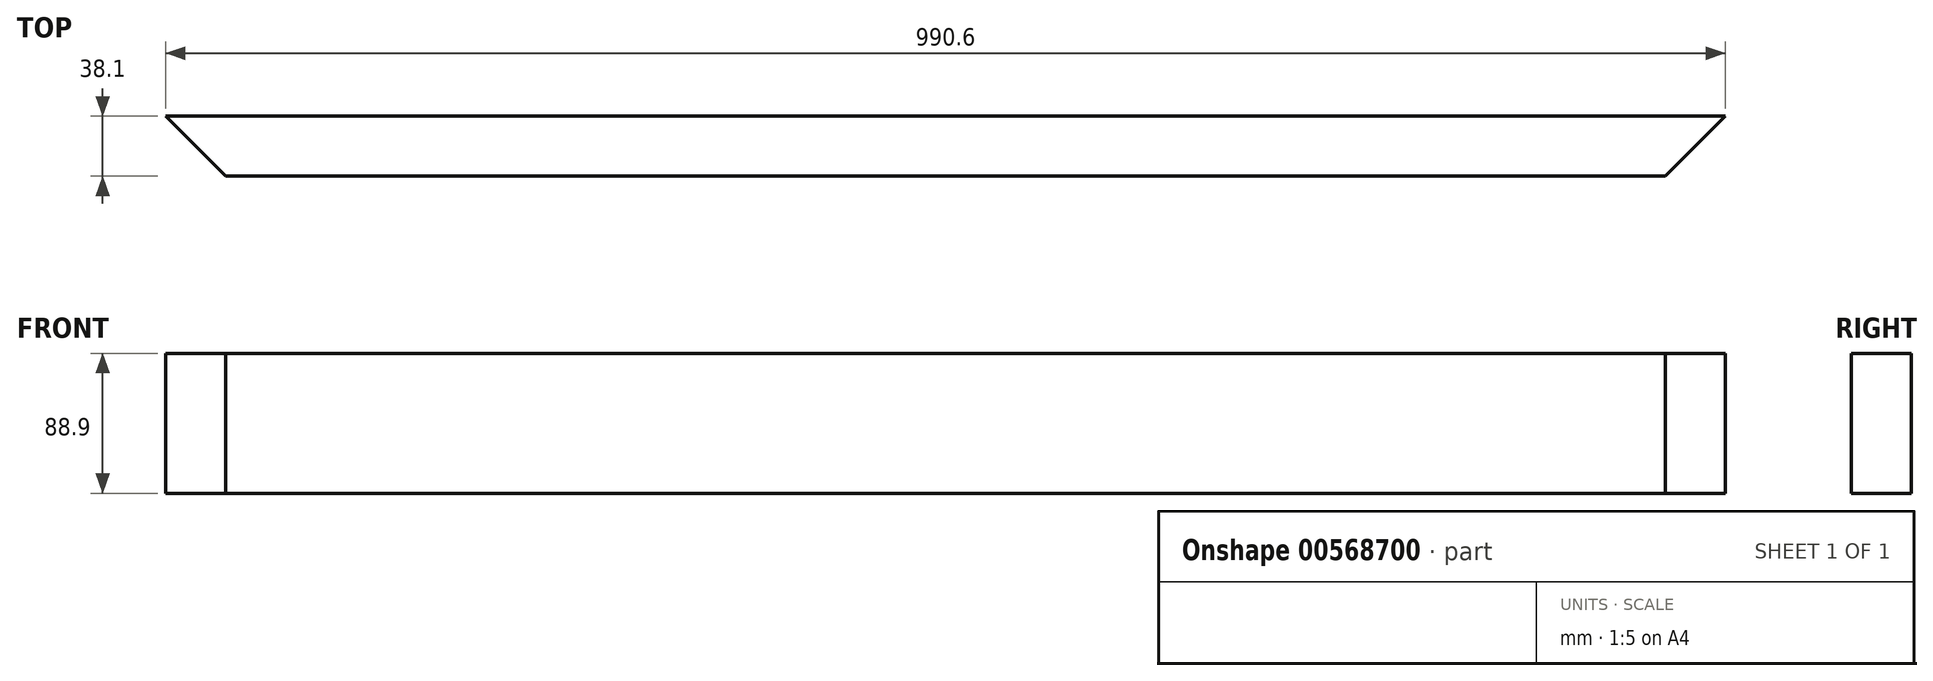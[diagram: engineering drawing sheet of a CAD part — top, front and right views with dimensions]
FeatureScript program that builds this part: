
annotation { "Feature Type Name" : "Feature", "Feature Type Description" : "" }
export const myFeature = defineFeature(function(context is Context, id is Id, definition is map)
    precondition{}
    {
        {
            var Q0;
            Q0=qCreatedBy(makeId("Front.planeOp"),FACE);
            var sketch = newSketch(context, id + "F0", { "sketchPlane" : qUnion([Q0])});
            skLineSegment(sketch, "E0.bottom", {"start": v(-495.3, -44.45) * mm, "end": v(495.3, -44.45) * mm});
            skLineSegment(sketch, "E0.top", {"start": v(-495.3, 44.45) * mm, "end": v(495.3, 44.45) * mm});
            skLineSegment(sketch, "E0.left", {"start": v(-495.3, -44.45) * mm, "end": v(-495.3, 44.45) * mm});
            skLineSegment(sketch, "E0.right", {"start": v(495.3, -44.45) * mm, "end": v(495.3, 44.45) * mm});
            skPoint(sketch, "E0.middle", {"position": v(0, 0) * mm});
            skSolve(sketch);
        }
        {
            var Q0;
            Q0 = qSketchRegion(id + "F0", true);
            extrude(context, id + "F1", {"entities" : qUnion([Q0]), "depth" : 38.1 * mm, "offsetDistance" : 25.4 * mm});
        }
        {
            var Q0;
            Q0=makeQuery(id+"F1.opExtrude","SWEPT_FACE",FACE,{"disambiguationData":[OSD([sQuery(id+"F0.wireOp",EDGE,"E0.top")])]});
            var sketch = newSketch(context, id + "F2", { "sketchPlane" : qUnion([Q0])});
            skLineSegment(sketch, "E1", {"start": v(-495.3, 0) * mm, "end": v(-457.2, -38.1) * mm});
            skLineSegment(sketch, "E2", {"start": v(-457.2, -38.1) * mm, "end": v(-495.3, -38.1) * mm});
            skLineSegment(sketch, "E3", {"start": v(-495.3, -38.1) * mm, "end": v(-495.3, 0) * mm});
            skLineSegment(sketch, "E4", {"start": v(495.3, 0) * mm, "end": v(457.2, -38.1) * mm});
            skLineSegment(sketch, "E5", {"start": v(457.2, -38.1) * mm, "end": v(495.3, -38.1) * mm});
            skLineSegment(sketch, "E6", {"start": v(495.3, -38.1) * mm, "end": v(495.3, 0) * mm});
            skSolve(sketch);
        }
        {
            var Q0;
            Q0 = qSketchRegion(id + "F2", true);
            extrude(context, id + "F3", {"entities" : qUnion([Q0]), "operationType" : NewBodyOperationType.REMOVE, "endBound" : BoundingType.THROUGH_ALL, "oppositeDirection" : true, "depth" : 25.4 * mm, "offsetDistance" : 25.4 * mm});
        }
    });
